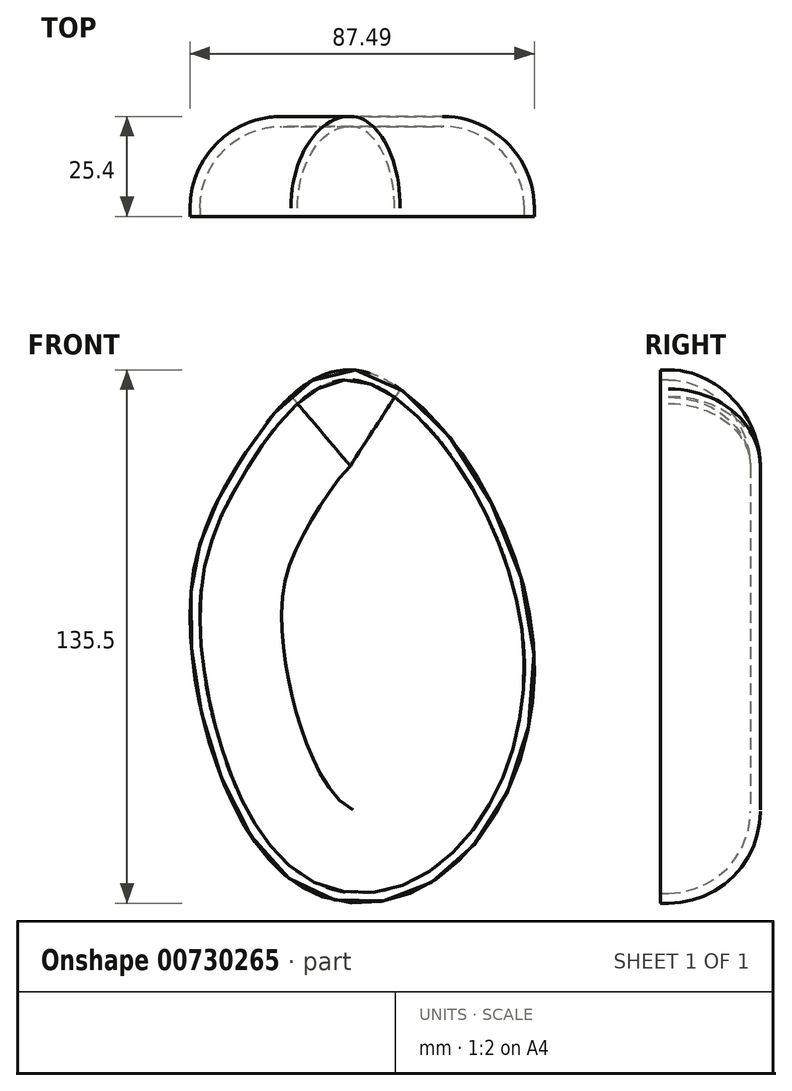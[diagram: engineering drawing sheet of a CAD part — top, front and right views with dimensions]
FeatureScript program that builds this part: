
annotation { "Feature Type Name" : "Feature", "Feature Type Description" : "" }
export const myFeature = defineFeature(function(context is Context, id is Id, definition is map)
    precondition{}
    {
        {
            var Q0;
            Q0=qCreatedBy(makeId("Front.planeOp"),FACE);
            var sketch = newSketch(context, id + "F0", { "sketchPlane" : qUnion([Q0])});
            skFitSpline(sketch, "E0", {"points": [v(0, 64.17) * mm, v(-30.25, 39.5) * mm, v(-42, 0) * mm, v(-18.5, -63.58) * mm, v(20.26, -65.35) * mm, v(44.64, 0) * mm, v(0, 64.17) * mm]});
            skSolve(sketch);
        }
        {
            var Q0;
            Q0=makeQuery(id+"F0.imprint","IMPRINT",FACE,{"disambiguationData":[TD([[makeQuery(id+"F0.imprint","IMPRINT",EDGE,{"derivedFrom":sQuery(id+"F0.wireOp",EDGE,"E0")}),1.0]])]});
            extrude(context, id + "F1", {"entities" : qUnion([Q0]), "endBound" : BoundingType.SYMMETRIC, "depth" : 25.4 * mm, "offsetDistance" : 25.4 * mm});
        }
        {
            var Q0;
            Q0=makeQuery(id+"F1.opExtrude","CAP_EDGE",EDGE,{"disambiguationData":[OSD([sQuery(id+"F0.wireOp",EDGE,"E0")])],"isStart":true});
            fillet(context, id + "F2", {"entities" : qUnion([Q0]), "radius" : 23.3 * mm, "tangentPropagation" : true, "allowEdgeOverflow" : false});
        }
        {
            var Q0;
            Q0=makeQuery(id+"F1.opExtrude","CAP_FACE",FACE,{"disambiguationData":[OSD([sQuery(id+"F0.wireOp",EDGE,"E0")])],"isStart":false});
            shell(context, id + "F3", {"entities" : qUnion([Q0]), "thickness" : 2.54 * mm});
        }
    });
